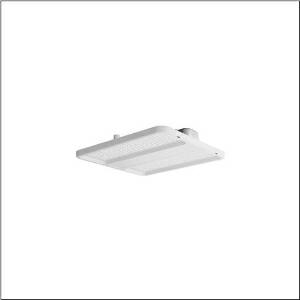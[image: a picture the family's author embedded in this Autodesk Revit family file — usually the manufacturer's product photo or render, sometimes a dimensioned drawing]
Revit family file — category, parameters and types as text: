
# Revit family: highbay_21_midi_52hn12da4lda
name_source: partatom
category: Lighting Fixtures
units: mm (PartAtom-declared; Revit-internal decimal feet)

## family parameters
Cut with Voids When Loaded = No
Host = Face
Light Source = No
Part Type = Normal
Room Calculation Point = No
Round Connector Dimension = Use Diameter
Shared = No

## types (1)
- --- (1 x LED, 4160 lm, 22.3 W, 4000K)
    Apparent Load = 22 VA
    CIE Flux Codes = 90 98 100 100 100
    Color Rendering = 80
    Color Temperature = 4000K
    Default Elevation = 1800 mm
    Description = high bay luminaire Highbay 21 midi; direct symmetric wide distribution, light control with lens of PMMA; UGR ≤ 22 (X = 4H | Y = 8H | S = 0.25H | reflection values 70/50/20); luminous flux: 26.500lm; light colour: 840, colour temperature: 4000K, MacAdam ≤ 3 SDCM (initial), colour rendering: CRI > 80; luminous efficacy: 185,8lm/W; rated service life: 75.000h (L80/B50) at AT= ta max; control: DALI 2; housing frame of high-performance plastic PA6, matt traffic white (RAL 9016); cover of PMMA; dimension (LxWxH): 474 x 442 x 72mm; luminaire connection: terminal, 5-pole, max. 2.5mm² (cable entry for one cable, Ø 8.5..16mm); mains connection: 230..240V, AC/DC 0/50..60Hz; connected load: 142,6W; protection rating (complete): IP66; insulation class (complete): insulation class I (protective earthing); protection symbol: D; impact resistance: IK08; halogen-free wiring; for central battery installations according to DIN EN 60598-2-22; LABS conformity tested according to VDMA 24364:2018-05; corresponds to IFS (International Featured Standards) requirements for safety and quality in the food industry; certification: CE, ENEC, VDE, UKCA; permissible operating ambient temperature: -40..+55°C (reducing of maximum allowable ambient temperature of 5°C with ceiling mounting); packaging unit: 1 piece; (delivery without accessories; please order mounting accessories separately)
    Height = 72 mm  [stored 0.23622 ft]
    Lamp = 1 x LED
    Lamp Light Flux = 4160 lm
    Lamp Power = 22.3 W
    Lamp count = 1
    Length = 474 mm
    Luminous efficacy = 187 lm/W
    Manufacturer = Siteco
    ModVariant = No
    Model = 52HN12DA4LDA
    Mounting Place = Ceiling
    Mounting Type = Pendant
    Number of Poles = 1
    OnlyDefault = Yes
    Power Factor = 1
    Product Name = Highbay 21 midi
    Product group = high bay luminaire
    ProductGroupID = 901
    Protection Class = Protection class I
    Protection Degree = IP 66
    RLX_Detail_Level = 1
    RLX_Emergency_Light_Flux = 0 lm
    RLX_Emergency_Type = 0
    RLX_Emergency_Type_DB = No
    RlxData = <blob elided: 17553 chars, md5=ffacd550>
    Socket = socket
    Standby Power = 0 W
    System Light Flux = 4160 lm
    System Power = 22 W
    Type Comments = : DC mode (central or group accumulator) initial emergency light level
    Type Image = l_1363240.jpg
    URL = http://relux.com
    VarID = @adj_000565
    Voltage = 0 V
    Weight = 0.00 kg
    Width = 442 mm

note: [stored X ft] marks values corroborated as IEEE doubles in the binary element streams (Revit-internal decimal feet)

## geometry (parser evidence)
native form markers: Blend x4, Sweep x11
no freeform markers — native parametric forms only
